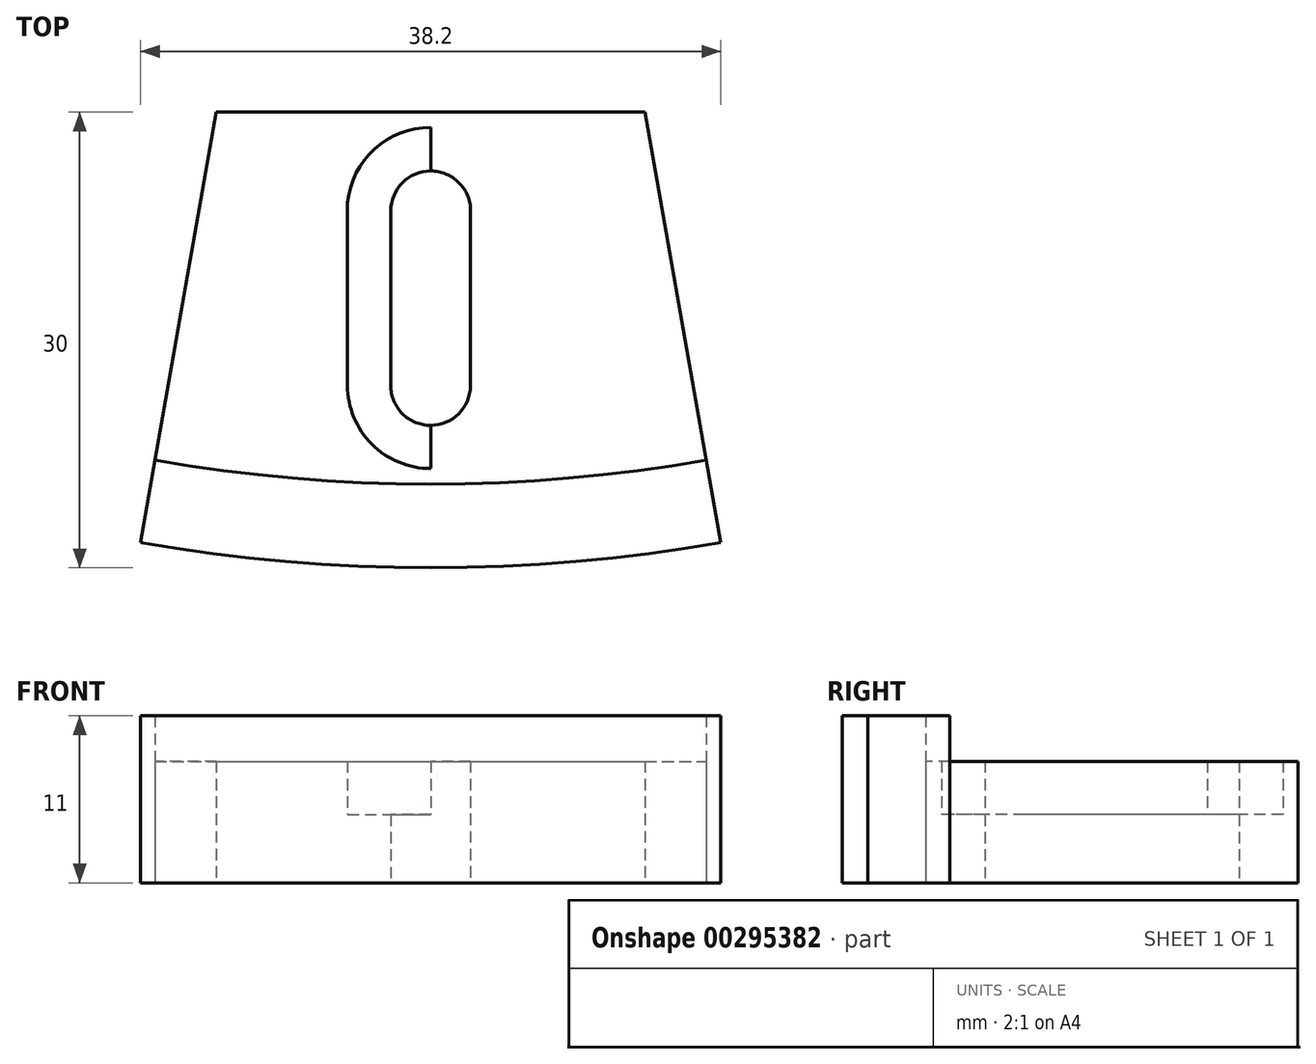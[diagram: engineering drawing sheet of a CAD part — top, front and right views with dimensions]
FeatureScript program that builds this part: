
annotation { "Feature Type Name" : "Feature", "Feature Type Description" : "" }
export const myFeature = defineFeature(function(context is Context, id is Id, definition is map)
    precondition{}
    {
        {
            var Q0;
            Q0=qCreatedBy(makeId("Top.planeOp"),FACE);
            var sketch = newSketch(context, id + "F0", { "sketchPlane" : qUnion([Q0])});
            skCircle(sketch, "E0", {"center": v(0, 0) * mm, "radius": 110 * mm});
            skLineSegment(sketch, "E1", {"start": v(0, 0) * mm, "end": v(19.1, -108.33) * mm});
            skLineSegment(sketch, "E2", {"start": v(0, 0) * mm, "end": v(-19.1, -108.33) * mm});
            skLineSegment(sketch, "E3", {"start": v(-14.1, -80) * mm, "end": v(14.1, -80) * mm});
            skCircle(sketch, "E4", {"center": v(0, 0) * mm, "radius": 104.5 * mm});
            skLineSegment(sketch, "E5", {"start": v(0, 0) * mm, "end": v(0, -110) * mm});
            skPoint(sketch, "E5.endSnap0", {"position": v(0, -80) * mm});
            skLineSegment(sketch, "E6", {"start": v(5.47, -85.97) * mm, "end": v(5.46, -98) * mm});
            skLineSegment(sketch, "E7", {"start": v(-5.47, -85.97) * mm, "end": v(-5.47, -98) * mm});
            skArc(sketch, "E8.trimOffspring", {"start": v(5.47, -85.97) * mm, "mid": v(0, -81) * mm, "end": v(-5.47, -85.97) * mm});
            skArc(sketch, "E9.trimOffspring", {"start": v(-5.47, -98) * mm, "mid": v(0, -103.47) * mm, "end": v(5.46, -98) * mm});
            skCircle(sketch, "E10", {"center": v(0, -86.5) * mm, "radius": 2.62 * mm});
            skCircle(sketch, "E11", {"center": v(0, -98) * mm, "radius": 2.62 * mm});
            skLineSegment(sketch, "E12", {"start": v(-2.63, -86.5) * mm, "end": v(-2.63, -98) * mm});
            skLineSegment(sketch, "E13", {"start": v(2.62, -98) * mm, "end": v(2.62, -86.5) * mm});
            skSolve(sketch);
        }
        {
            var Q0;
            {var subQ0=sQuery(id+"F0.wireOp",EDGE,"E1");var subQ1=sQuery(id+"F0.wireOp",EDGE,"E0");var subQ2=makeQuery(id+"F0.imprint","INTERSECT",VERTEX,{"derivedFrom":[subQ1,subQ0]});Q0=makeQuery(id+"F0.imprint","IMPRINT",FACE,{"disambiguationData":[TD([[makeQuery(id+"F0.imprint","IMPRINT",EDGE,{"disambiguationData":[TD([[subQ2,1.0]])],"derivedFrom":subQ1}),1.0]])]});}
            var Q1;
            {var subQ0=sQuery(id+"F0.wireOp",EDGE,"E2");var subQ1=sQuery(id+"F0.wireOp",EDGE,"E0");var subQ2=makeQuery(id+"F0.imprint","INTERSECT",VERTEX,{"derivedFrom":[subQ1,subQ0]});Q1=makeQuery(id+"F0.imprint","IMPRINT",FACE,{"disambiguationData":[TD([[makeQuery(id+"F0.imprint","IMPRINT",EDGE,{"disambiguationData":[TD([[subQ2,-1.0]])],"derivedFrom":subQ1}),1.0]])]});}
            extrude(context, id + "F1", {"entities" : qUnion([Q0, Q1]), "offsetDistance" : 25 * mm, "depth" : 11 * mm});
        }
        {
            var Q0;
            {var subQ12=sQuery(id+"F0.wireOp",EDGE,"E7");Q0=makeQuery(id+"F0.imprint","IMPRINT",FACE,{"disambiguationData":[TD([[makeQuery(id+"F0.imprint","IMPRINT",EDGE,{"derivedFrom":subQ12}),-1.0]])]});}
            var Q1;
            {var subQ5=sQuery(id+"F0.wireOp",EDGE,"E6");Q1=makeQuery(id+"F0.imprint","IMPRINT",FACE,{"disambiguationData":[TD([[makeQuery(id+"F0.imprint","IMPRINT",EDGE,{"derivedFrom":subQ5}),1.0]])]});}
            var Q2;
            {var subQ0=sQuery(id+"F0.wireOp",EDGE,"NUf4yNpD-Tuvc-Y5Yg-kzcZ-NHsfBDEtUA5E");Q2=makeQuery(id+"F0.imprint","IMPRINT",FACE,{"disambiguationData":[TD([[makeQuery(id+"F0.imprint","IMPRINT",EDGE,{"derivedFrom":subQ0}),-1.0]])]});}
            var Q3;
            {var subQ0=sQuery(id+"F0.wireOp",EDGE,"pz7i9jfQ-Zu1g-DyQ0-b1Z4-iFR7DHlQGjnN");Q3=makeQuery(id+"F0.imprint","IMPRINT",FACE,{"disambiguationData":[TD([[makeQuery(id+"F0.imprint","IMPRINT",EDGE,{"derivedFrom":subQ0}),1.0]])]});}
            var Q4;
            {var subQ6=sQuery(id+"F0.wireOp",EDGE,"pz7i9jfQ-Zu1g-DyQ0-b1Z4-iFR7DHlQGjnN");Q4=makeQuery(id+"F0.imprint","IMPRINT",FACE,{"disambiguationData":[TD([[makeQuery(id+"F0.imprint","IMPRINT",EDGE,{"derivedFrom":subQ6}),-1.0]])]});}
            var Q5;
            {var subQ4=sQuery(id+"F0.wireOp",EDGE,"7J0IRvuI-Yc04-S6jk-2BbN-LaUVp6ymkvtD");Q5=makeQuery(id+"F0.imprint","IMPRINT",FACE,{"disambiguationData":[TD([[makeQuery(id+"F0.imprint","IMPRINT",EDGE,{"derivedFrom":subQ4}),-1.0]])]});}
            var Q6;
            {var subQ1=sQuery(id+"F0.wireOp",EDGE,"E5");var subQ4=sQuery(id+"F0.wireOp",EDGE,"NXPRGXRv-MdXg-5Vgw-CKrY-bQkwvO6CI4ft");var subQ5=makeQuery(id+"F0.imprint","INTERSECT",VERTEX,{"derivedFrom":[subQ1,subQ4]});Q6=makeQuery(id+"F0.imprint","IMPRINT",FACE,{"disambiguationData":[TD([[makeQuery(id+"F0.imprint","IMPRINT",EDGE,{"disambiguationData":[TD([[subQ5,-1.0]])],"derivedFrom":subQ1}),1.0]])]});}
            var Q7;
            {var subQ5=sQuery(id+"F0.wireOp",EDGE,"E7");Q7=makeQuery(id+"F0.imprint","IMPRINT",FACE,{"disambiguationData":[TD([[makeQuery(id+"F0.imprint","IMPRINT",EDGE,{"derivedFrom":subQ5}),-1.0]])]});}
            extrude(context, id + "F2", {"entities" : qUnion([Q0, Q1, Q2, Q3, Q4, Q5, Q6, Q7]), "offsetDistance" : 25 * mm, "depth" : 8 * mm});
        }
        {
            var Q0;
            {var subQ0=sQuery(id+"F0.wireOp",EDGE,"a4SDoGBH-Mrsk-hmo4-jYc1-8lZoNV2MiLsw");Q0=makeQuery(id+"F0.imprint","IMPRINT",FACE,{"disambiguationData":[TD([[makeQuery(id+"F0.imprint","IMPRINT",EDGE,{"derivedFrom":subQ0}),-1.0]])]});}
            var Q1;
            {var subQ13=sQuery(id+"F0.wireOp",EDGE,"83adfd88-321e-4995-af4e-37a7658b469b.trimOffspring");Q1=makeQuery(id+"F0.imprint","IMPRINT",FACE,{"disambiguationData":[TD([[makeQuery(id+"F0.imprint","IMPRINT",EDGE,{"derivedFrom":subQ13}),-1.0]])]});}
            var Q2;
            {var subQ0=sQuery(id+"F0.wireOp",EDGE,"E7");Q2=makeQuery(id+"F0.imprint","IMPRINT",FACE,{"disambiguationData":[TD([[makeQuery(id+"F0.imprint","IMPRINT",EDGE,{"derivedFrom":subQ0}),1.0]])]});}
            var Q3;
            {var subQ0=sQuery(id+"F0.wireOp",EDGE,"E6");Q3=makeQuery(id+"F0.imprint","IMPRINT",FACE,{"disambiguationData":[TD([[makeQuery(id+"F0.imprint","IMPRINT",EDGE,{"derivedFrom":subQ0}),-1.0]])]});}
            extrude(context, id + "F3", {"entities" : qUnion([Q0, Q1, Q2, Q3]), "operationType" : NewBodyOperationType.ADD, "offsetDistance" : 25 * mm, "depth" : 4.5 * mm});
        }
    });
